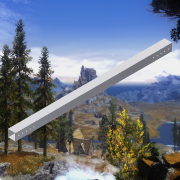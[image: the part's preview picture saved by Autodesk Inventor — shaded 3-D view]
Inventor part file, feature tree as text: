
AUTODESK INVENTOR PART (.ipt)
format: ipt  version: 2015 SP1 (Build 190203100, 203)  size: 218,112 bytes
history: native  units: in
note: dims shown in document units (in); Inventor stores cm internally (conversion verified against a paired STEP export)
features: sketch x4, extrude x3, reference x2, hole x1, plane x1
ambient origin geometry x8: Origin, YZ Plane, XZ Plane, XY Plane, X Axis, Y Axis, Z Axis, Center Point
bodies: Solid1 (feature_tree)
feature tree (11):
  extrude  "Extrusion1"  Depth=1.0in
  hole  "Hole1"  [1 undecoded]
  extrude  "Extrusion5"  Depth=0.0625in
  plane  "Work Plane1"
  extrude  "Extrusion7"  Depth=1.0in TaperAngle=0.0deg
  sketch  "Sketch1"  dims[d0=1.0in d1=1.0in]
  sketch  "Sketch2"  dims[d6=0.125in d7=0.125in]
  reference  "Reference1"
  reference  "Reference2"
  sketch  "Sketch7"  dims[d8=26.0in d9=0.0in]
  sketch  "Sketch9"  dims[d10=0.163in d11=0.75in d12=0.375in d13=0.25in d14=0.5635in d15=1.0in d16=0.8108in d33=0.0625in d34=1.0in d35=0.0in d36=0.1875in d42=2.5in d43=2.5in d44=1.0in d45=0.0in]
note: 1 required parameter value undecoded (feature->parameter linkage not recoverable at this tier; creation-order binding heuristic only, values carry confidence <= 0.55)
